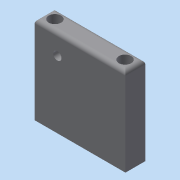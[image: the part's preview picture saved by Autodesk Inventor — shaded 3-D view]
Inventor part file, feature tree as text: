
AUTODESK INVENTOR PART (.ipt)
format: ipt  version: 2015 (Build 190159000, 159)  size: 103,936 bytes
history: native  units: mm
features: sketch x2, extrude x1, fillet x1, hole x1
ambient origin geometry x8: Origin, YZ Plane, XZ Plane, XY Plane, X Axis, Y Axis, Z Axis, Center Point
bodies: Solid1 (feature_tree)
feature tree (5):
  extrude  "Extrusion1"  Depth=6.0mm
  fillet  "Fillet1"  Radius=34.0mm
  hole  "Hole1"  [1 undecoded]
  sketch  "Sketch1"  dims[d0=6.0mm d1=6.0mm d2=34.0mm]
  sketch  "Sketch2"  dims[d3=44.0mm d4=5.0mm d5=42.5mm d6=0.0mm d7=2.0mm d10=4.0mm d11=6.0mm d12=4.0mm d13=2.0mm d14=90.0deg d15=10.0mm d16=20.594885mm d17=10.0mm d18=11.0mm]
note: 1 required parameter value undecoded (feature->parameter linkage not recoverable at this tier; creation-order binding heuristic only, values carry confidence <= 0.55)
